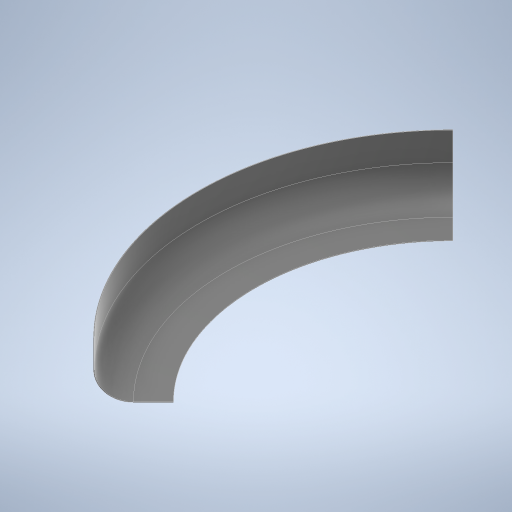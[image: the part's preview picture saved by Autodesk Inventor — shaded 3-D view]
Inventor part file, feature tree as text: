
AUTODESK INVENTOR PART (.ipt)
format: ipt  version: 2023.2 (Build 272271000, 271)  size: 292,352 bytes
history: native  units: mm
features: sketch x2, extrude x1, fillet x1, revolve x1
ambient origin geometry x8: Origin, YZ Plane, XZ Plane, XY Plane, X Axis, Y Axis, Z Axis, Center Point
bodies: Solid1 (feature_tree)
feature tree (5):
  extrude  "Extrusion1"  Depth=500.0mm
  fillet  "Fillet1"  Radius=10.0mm
  revolve  "Revolution1"  [1 undecoded]
  sketch  "Sketch1"  dims[d0=1000.0mm d1=500.0mm d2=10.0mm d3=0.0mm]
  sketch  "Sketch4"  dims[d4=2.0mm d17=500.0mm d18=10.0mm d19=1000.0mm d20=4000.0mm d21=90.0deg]
note: 1 required parameter value undecoded (feature->parameter linkage not recoverable at this tier; creation-order binding heuristic only, values carry confidence <= 0.55)
